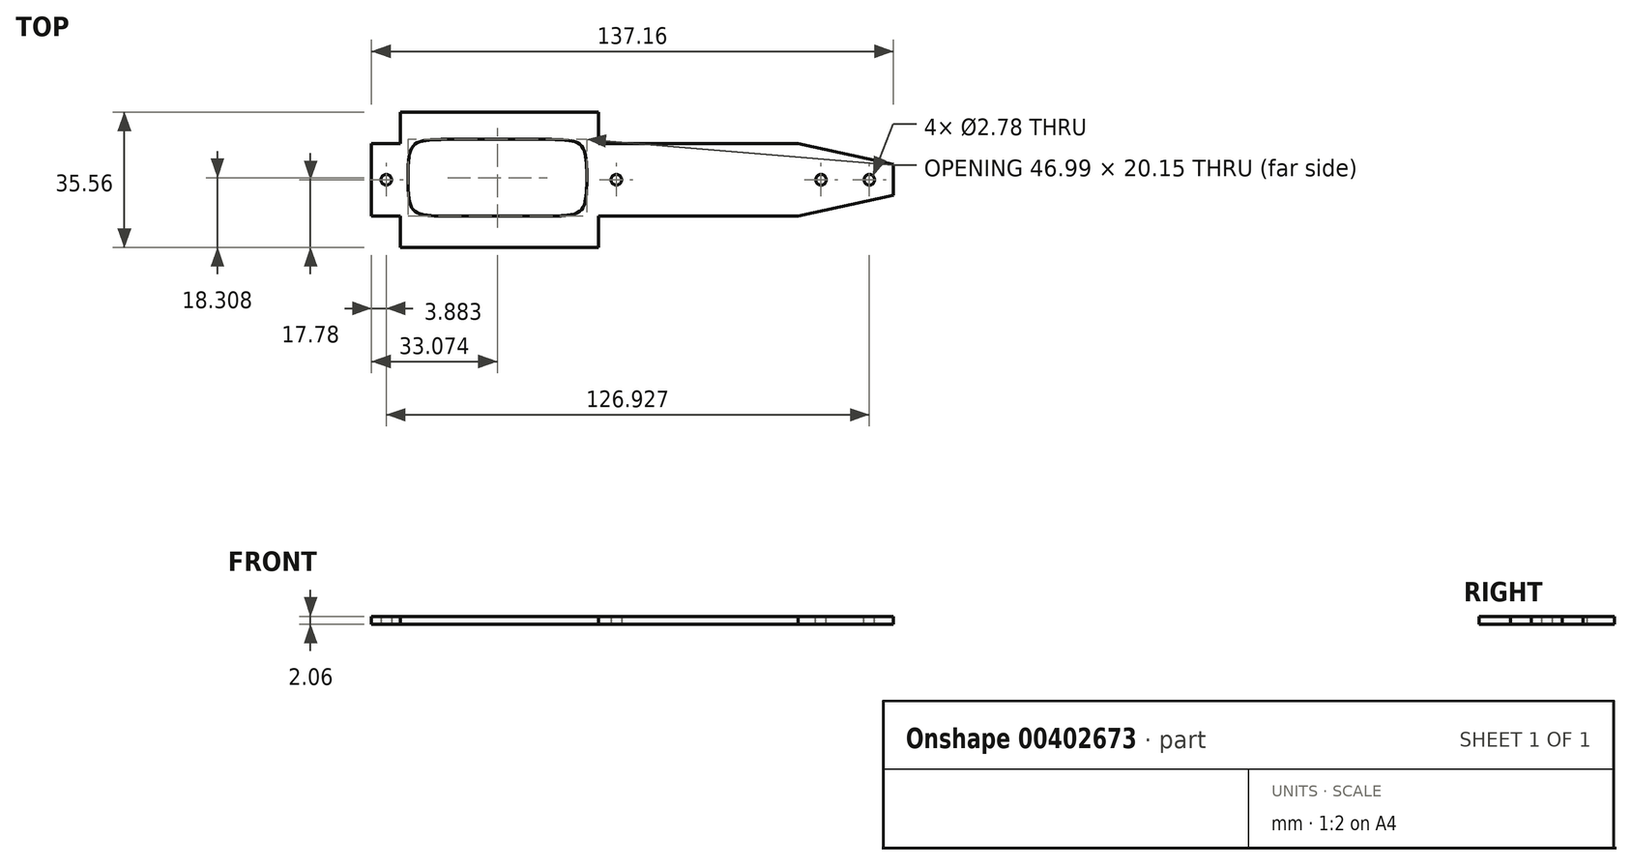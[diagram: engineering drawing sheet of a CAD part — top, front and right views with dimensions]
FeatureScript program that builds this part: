
annotation { "Feature Type Name" : "Feature", "Feature Type Description" : "" }
export const myFeature = defineFeature(function(context is Context, id is Id, definition is map)
    precondition{}
    {
        {
            var Q0;
            Q0=qCreatedBy(makeId("Top.planeOp"),FACE);
            var sketch = newSketch(context, id + "F0", { "sketchPlane" : qUnion([Q0])});
            skLineSegment(sketch, "E0.bottom", {"start": v(68.58, -9.52) * mm, "end": v(-68.58, -9.53) * mm});
            skLineSegment(sketch, "E0.top", {"start": v(68.58, 9.53) * mm, "end": v(-68.58, 9.52) * mm});
            skLineSegment(sketch, "E0.left", {"start": v(68.58, -9.52) * mm, "end": v(68.58, 9.53) * mm});
            skLineSegment(sketch, "E0.right", {"start": v(-68.58, -9.53) * mm, "end": v(-68.58, 9.53) * mm});
            skPoint(sketch, "E0.middle", {"position": v(0, 0) * mm});
            skLineSegment(sketch, "E1.bottom", {"start": v(-60.96, 17.78) * mm, "end": v(-8.9, 17.78) * mm});
            skLineSegment(sketch, "E1.top", {"start": v(-60.96, -17.78) * mm, "end": v(-8.9, -17.78) * mm});
            skLineSegment(sketch, "E1.left", {"start": v(-60.96, 17.78) * mm, "end": v(-60.96, -17.78) * mm});
            skLineSegment(sketch, "E1.right", {"start": v(-8.9, 17.78) * mm, "end": v(-8.9, -17.78) * mm});
            skPoint(sketch, "E1.middle", {"position": v(-34.93, 0) * mm});
            skCircle(sketch, "E2", {"center": v(-64.7, 0) * mm, "radius": 1.39 * mm});
            skPoint(sketch, "E2.centerSnap0", {"position": v(-60.96, 0) * mm});
            skCircle(sketch, "E3", {"center": v(-4.24, 0) * mm, "radius": 1.39 * mm});
            skSolve(sketch);
        }
        {
            var Q0;
            Q0 = qSketchRegion(id + "F0", true);
            extrude(context, id + "F1", {"entities" : qUnion([Q0]), "depth" : 2.06 * mm});
        }
        {
            var Q0;
            Q0=makeQuery(id+"F1.opExtrude","CAP_FACE",FACE,{"disambiguationData":[OSD([sQuery(id+"F0.wireOp",EDGE,"E0.bottom"),sQuery(id+"F0.wireOp",EDGE,"E0.top"),sQuery(id+"F0.wireOp",EDGE,"E0.left"),sQuery(id+"F0.wireOp",EDGE,"E0.right"),sQuery(id+"F0.wireOp",EDGE,"E1.bottom"),sQuery(id+"F0.wireOp",EDGE,"E1.top"),sQuery(id+"F0.wireOp",EDGE,"E1.left"),sQuery(id+"F0.wireOp",EDGE,"E1.right"),sQuery(id+"F0.wireOp",EDGE,"E2"),sQuery(id+"F0.wireOp",EDGE,"E3")])],"isStart":false});
            var sketch = newSketch(context, id + "F2", { "sketchPlane" : qUnion([Q0])});
            skLineSegment(sketch, "E4", {"start": v(68.58, 4.07) * mm, "end": v(43.56, 9.53) * mm});
            skLineSegment(sketch, "E5", {"start": v(43.56, 9.53) * mm, "end": v(68.58, 9.53) * mm});
            skLineSegment(sketch, "E6", {"start": v(68.58, 9.53) * mm, "end": v(68.58, 4.07) * mm});
            skLineSegment(sketch, "E7.MirrorCS", {"start": v(68.58, -4.07) * mm, "end": v(43.56, -9.53) * mm});
            skLineSegment(sketch, "E8.MirrorCS", {"start": v(43.56, -9.53) * mm, "end": v(68.58, -9.53) * mm});
            skCircle(sketch, "E9", {"center": v(62.23, 0) * mm, "radius": 1.39 * mm});
            skCircle(sketch, "E10", {"center": v(49.53, 0) * mm, "radius": 1.39 * mm});
            skLineSegment(sketch, "E11.bottom", {"start": v(-59, 10.6) * mm, "end": v(-12.01, 10.6) * mm});
            skLineSegment(sketch, "E11.top", {"start": v(-59, -9.55) * mm, "end": v(-12.01, -9.55) * mm});
            skLineSegment(sketch, "E11.left", {"start": v(-59, 10.6) * mm, "end": v(-59, -9.55) * mm});
            skLineSegment(sketch, "E11.right", {"start": v(-12.01, 10.6) * mm, "end": v(-12.01, -9.55) * mm});
            skSolve(sketch);
        }
        {
            var Q0;
            Q0=makeQuery(id+"F2.imprint","IMPRINT",FACE,{"disambiguationData":[TD([[makeQuery(id+"F2.imprint","IMPRINT",EDGE,{"derivedFrom":sQuery(id+"F2.wireOp",EDGE,"E4")}),-1.0]])]});
            var Q1;
            {var subQ0=sQuery(id+"F2.wireOp",EDGE,"E7.MirrorCS");Q1=makeQuery(id+"F2.imprint","IMPRINT",FACE,{"disambiguationData":[TD([[makeQuery(id+"F2.imprint","IMPRINT",EDGE,{"derivedFrom":subQ0}),1.0]])]});}
            var Q2;
            Q2=makeQuery(id+"F2.imprint","IMPRINT",FACE,{"disambiguationData":[TD([[makeQuery(id+"F2.imprint","IMPRINT",EDGE,{"derivedFrom":sQuery(id+"F2.wireOp",EDGE,"E10")}),1.0]])]});
            var Q3;
            Q3=makeQuery(id+"F2.imprint","IMPRINT",FACE,{"disambiguationData":[TD([[makeQuery(id+"F2.imprint","IMPRINT",EDGE,{"derivedFrom":sQuery(id+"F2.wireOp",EDGE,"E9")}),1.0]])]});
            var Q4;
            Q4=makeQuery(id+"F2.imprint","IMPRINT",FACE,{"disambiguationData":[TD([[makeQuery(id+"F2.imprint","IMPRINT",EDGE,{"derivedFrom":sQuery(id+"F2.wireOp",EDGE,"E11.bottom")}),-1.0]])]});
            extrude(context, id + "F3", {"entities" : qUnion([Q0, Q1, Q2, Q3, Q4]), "operationType" : NewBodyOperationType.REMOVE, "oppositeDirection" : true, "depth" : 25.4 * mm});
        }
        {
            var Q0;
            Q0=makeQuery(id+"F3.boolean.opBoolean","COPY",EDGE,{"derivedFrom":makeQuery(id+"F3.opExtrude","SWEPT_EDGE",EDGE,{"disambiguationData":[OSD([sQuery(id+"F2.wireOp",EDGE,"E11.bottom"),sQuery(id+"F2.wireOp",EDGE,"E11.right")])]})});
            var Q1;
            Q1=makeQuery(id+"F3.boolean.opBoolean","COPY",EDGE,{"derivedFrom":makeQuery(id+"F3.opExtrude","SWEPT_EDGE",EDGE,{"disambiguationData":[OSD([sQuery(id+"F2.wireOp",EDGE,"E11.bottom"),sQuery(id+"F2.wireOp",EDGE,"E11.left")])]})});
            var Q2;
            Q2=makeQuery(id+"F3.boolean.opBoolean","COPY",EDGE,{"derivedFrom":makeQuery(id+"F3.opExtrude","SWEPT_EDGE",EDGE,{"disambiguationData":[OSD([sQuery(id+"F2.wireOp",EDGE,"E11.top"),sQuery(id+"F2.wireOp",EDGE,"E11.left")])]})});
            var Q3;
            Q3=makeQuery(id+"F3.boolean.opBoolean","COPY",EDGE,{"derivedFrom":makeQuery(id+"F3.opExtrude","SWEPT_EDGE",EDGE,{"disambiguationData":[OSD([sQuery(id+"F2.wireOp",EDGE,"E11.top"),sQuery(id+"F2.wireOp",EDGE,"E11.right")])]})});
            fillet(context, id + "F4", {"entities" : qUnion([Q0, Q1, Q2, Q3]), "radius" : 10.16 * mm, "tangentPropagation" : true, "rho" : .7, "crossSection" : FilletCrossSection.CONIC, "allowEdgeOverflow" : false});
        }
    });
